# Revit family: Spout-GROHE-Universal-13611000_Series
name_source: partatom
category: Plumbing Fixtures
units: mm (PartAtom-declared; Revit-internal decimal feet)

## family parameters
Cut with Voids When Loaded = No
Host = Face
OmniClass Number = 23.45.05.14.17
OmniClass Title = Showers
Part Type = Normal
Room Calculation Point = No
Round Connector Dimension = Use Diameter
Shared = Yes

## types (2) — shared parameters
Assembly Code = D2020300
CW Connection = Yes
CWFU = 3
Default Elevation = 21"
Description = Wall mounted spout with diverter
HW Connection = Yes
HWFU = 3
Installation Type = Wall Mounted
Length = 5 1/2"
Manufacturer = Grohe
Price = Prices may vary. Please consult Manufacturer Representative for most up-to-date price list.
Product Documentation Link = https://americanstandard.box.com
URL = https://www.grohe.us
Vent Connection = No
WFU = 4
Warranty Information = Limited Lifetime Function and Finish Warranty
Waste Connection = Yes
Water Connection Diameter = 1/2"
Water Connection Radius = 1/4"
Width = 2 1/2"

## per-type parameters (varying)
| type | Finish | Material | Product Page URL |
| 13611000 | Metal-Grohe-000-Polished Chrome | Metal-Grohe-000-Polished Chrome | https://www.grohe.us |
| 13611EN0 | Metal-Grohe-EN0-Brushed Nickel | Metal-Grohe-EN0-Brushed Nickel | https://www.grohe.ca |

note: column(s) folded — value = type name in every type: Model

## geometry (parser evidence)
native form markers: Sweep x3
no freeform markers — native parametric forms only
